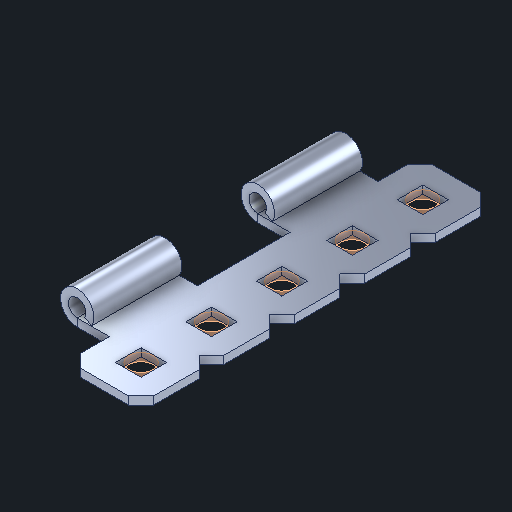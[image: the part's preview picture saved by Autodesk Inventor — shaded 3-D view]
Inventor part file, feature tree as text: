
AUTODESK INVENTOR PART (.ipt)
format: ipt  version: 2024 (Build 280153000, 153)  size: 240,640 bytes
history: native  units: in
note: dims shown in document units (in); Inventor stores cm internally (conversion verified against a paired STEP export)
features: other x14, sketch x1
ambient origin geometry x8: Origin, YZ Plane, XZ Plane, XY Plane, X Axis, Y Axis, Z Axis, Center Point
bodies: Body1 (feature_tree), Body2 (feature_tree), Body3 (feature_tree), Body4 (feature_tree), Body5 (feature_tree), Body6 (feature_tree)
feature tree (15):
  other  "Bottom 5.ipt"
  other  "Cut-Extrude3::Bottom 5.ipt"
  other  "TaggingFeature1"
  sketch  "Sketch1"  dims[d0=0.3937in]
  other  "Srf1"
  other  "Srf2"
  other  "Srf3"
  other  "Srf4"
  other  "Srf5"
  other  "Cut-Extrude3"
  other  "Srf1::Derived"
  other  "Srf2::Derived"
  other  "Srf3::Derived"
  other  "Srf4::Derived"
  other  "Srf5::Derived"
